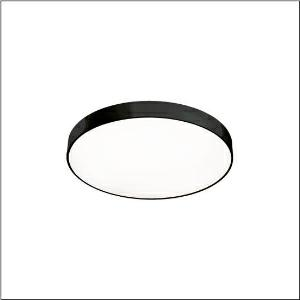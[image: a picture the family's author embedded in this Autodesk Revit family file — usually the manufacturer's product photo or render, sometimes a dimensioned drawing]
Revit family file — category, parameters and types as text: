
# Revit family: round_21_m_51mr36gm8321b
name_source: partatom
category: Lighting Fixtures
units: mm (PartAtom-declared; Revit-internal decimal feet)

## family parameters
Cut with Voids When Loaded = No
Host = Face
Light Source = No
Part Type = Normal
Room Calculation Point = No
Round Connector Dimension = Use Diameter
Shared = No

## types (1)
- --- (1 x LED, 7820 lm, 60.8 W, 3000K)
    Apparent Load = 61 VA
    CIE Flux Codes = 49 80 96 85 100
    Color Rendering = 80
    Color Temperature = 3000K
    Default Elevation = 1800 mm
    Description = Round 21 M, wall and ceiling luminaire, primary optical cover: cover, of PMMA, opal, light emission: direct/indirect distribution, primary light characteristic: symmetric, installation type: suspended mounting, surface-mounted, LED, rated luminous flux: 7.820lm, luminous efficacy: 129lm/W, light colour: 830, colour temperature: 3000K, with terminal, 3-pole, mains connection: 230V, AC, 50/60Hz, rated input power: 61W, housing, of aluminium, coated, black, diameter: 600mm, height: 62mm, protection rating (complete): IP40, insulation class (complete): insulation class I (protective earthing), certification: CE, impact resistance: IK04, permissible operating ambient temperature: -10..+35°C, packaging unit: 1 piece
    Height = 87 mm
    Lamp = 1 x LED
    Lamp Light Flux = 7820 lm
    Lamp Power = 60.8 W
    Lamp count = 1
    Length = 600 mm
    Luminous efficacy = 129 lm/W
    Manufacturer = Siteco
    ModVariant = No
    Model = 51MR36GM8321B
    Mounting Place = Ceiling
    Mounting Type = Surface mounted
    Number of Poles = 1
    OnlyDefault = Yes
    Power Factor = 1
    Product Name = Round 21 M
    Product group = wall and ceiling luminaire
    ProductGroupID = 302
    Protection Class = Protection class I
    Protection Degree = IP 40
    RLX_Detail_Level = 1
    RLX_Emergency_Light_Flux = 0 lm
    RLX_Emergency_Type = 0
    RLX_Emergency_Type_DB = No
    RlxData = <blob elided: 20769 chars, md5=26d81715>
    Socket = socket
    Standby Power = 0 W
    System Light Flux = 7820 lm
    System Power = 61 W
    Type Comments = factory setting: luminous flux: 100 % | (ON | ON | ON | ON) | 700 mA
    Type Image = l_1258332.jpg
    URL = http://relux.com
    VarID = @adj_031855
    Voltage = 0 V
    Weight = 0.00 kg
    Width = 0 mm  [stored 0 ft]

note: [stored X ft] marks values corroborated as IEEE doubles in the binary element streams (Revit-internal decimal feet)

## geometry (parser evidence)
native form markers: Blend x4, Sweep x11
no freeform markers — native parametric forms only
